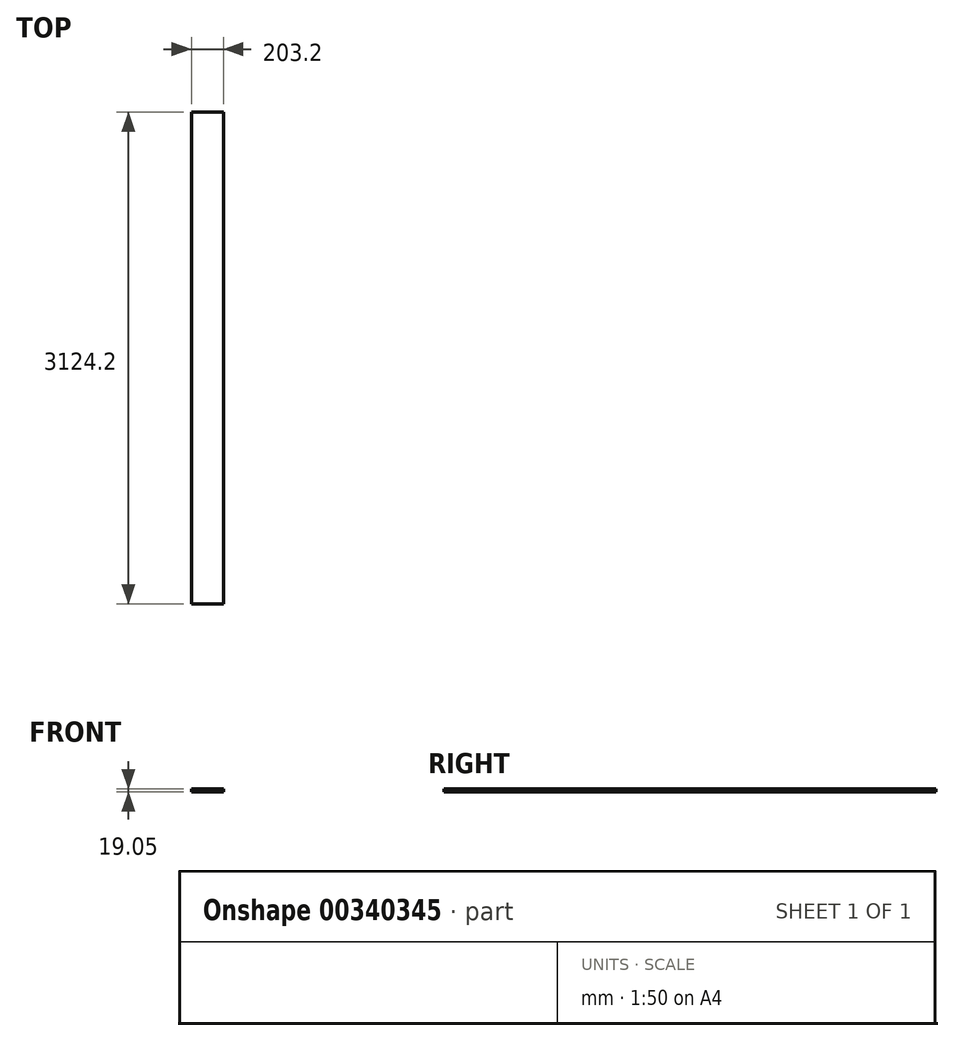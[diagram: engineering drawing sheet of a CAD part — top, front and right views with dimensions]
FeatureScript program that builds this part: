
annotation { "Feature Type Name" : "Feature", "Feature Type Description" : "" }
export const myFeature = defineFeature(function(context is Context, id is Id, definition is map)
    precondition{}
    {
        {
            var Q0;
            Q0=qCreatedBy(makeId("Top.planeOp"),FACE);
            var sketch = newSketch(context, id + "F0", { "sketchPlane" : qUnion([Q0])});
            skLineSegment(sketch, "E0.bottom", {"start": v(101.6, 1562.1) * mm, "end": v(-101.6, 1562.1) * mm});
            skLineSegment(sketch, "E0.top", {"start": v(101.6, -1562.1) * mm, "end": v(-101.6, -1562.1) * mm});
            skLineSegment(sketch, "E0.left", {"start": v(101.6, 1562.1) * mm, "end": v(101.6, -1562.1) * mm});
            skLineSegment(sketch, "E0.right", {"start": v(-101.6, 1562.1) * mm, "end": v(-101.6, -1562.1) * mm});
            skPoint(sketch, "E0.middle", {"position": v(0, 0) * mm});
            skSolve(sketch);
        }
        {
            var Q0;
            Q0=makeQuery(id+"F0.imprint","IMPRINT",FACE,{"disambiguationData":[TD([[makeQuery(id+"F0.imprint","IMPRINT",EDGE,{"derivedFrom":sQuery(id+"F0.wireOp",EDGE,"E0.bottom")}),1.0]])]});
            extrude(context, id + "F1", {"entities" : qUnion([Q0]), "depth" : 19.05 * mm});
        }
    });
